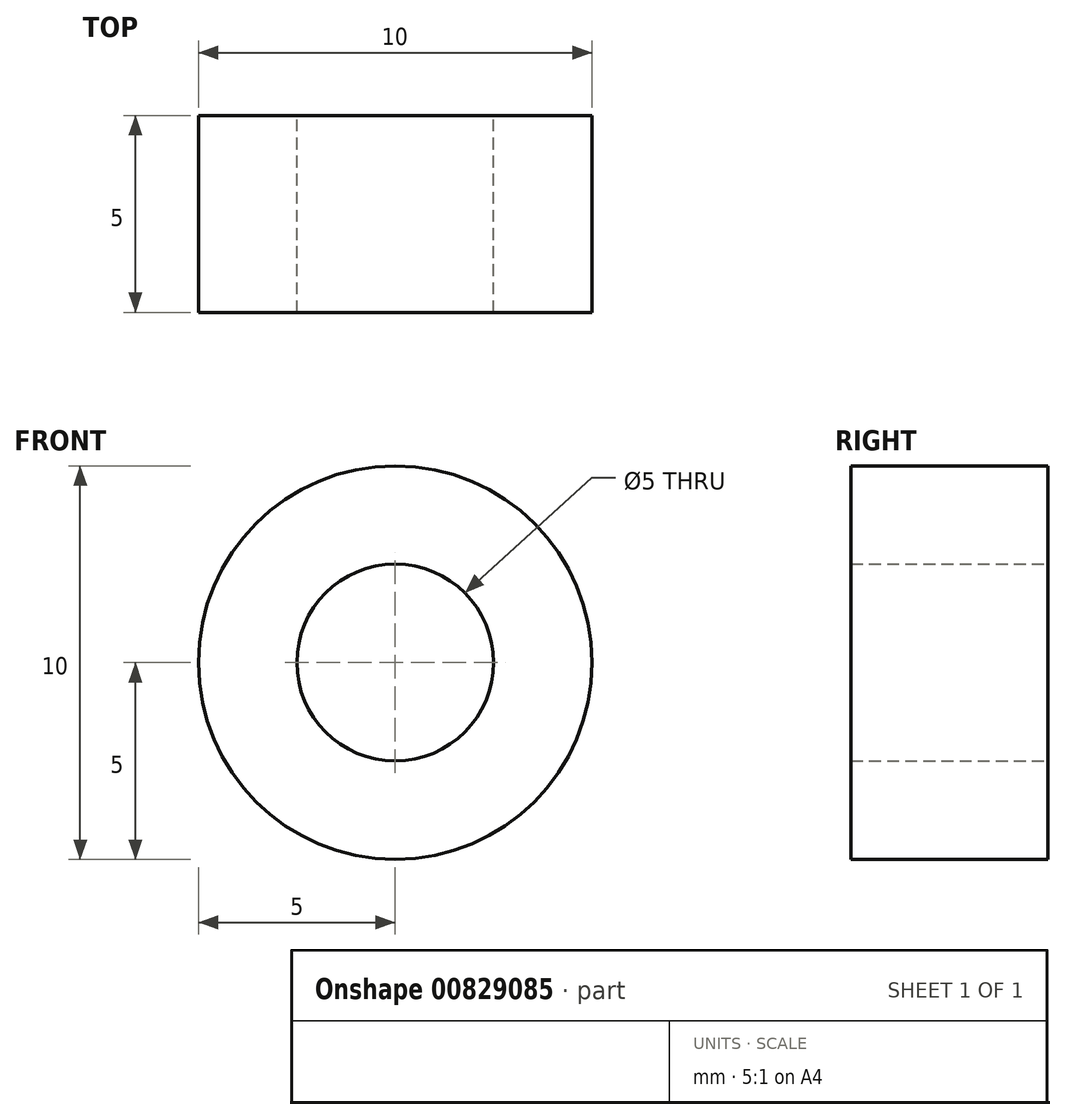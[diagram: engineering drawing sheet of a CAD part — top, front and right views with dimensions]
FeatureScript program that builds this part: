
annotation { "Feature Type Name" : "Feature", "Feature Type Description" : "" }
export const myFeature = defineFeature(function(context is Context, id is Id, definition is map)
    precondition{}
    {
        {
            var Q0;
            Q0=qCreatedBy(makeId("Front.planeOp"),FACE);
            var sketch = newSketch(context, id + "F0", { "sketchPlane" : qUnion([Q0])});
            skCircle(sketch, "E0", {"center": v(0, 0) * mm, "radius": 5 * mm});
            skCircle(sketch, "E1", {"center": v(0, 0) * mm, "radius": 2.5 * mm});
            skSolve(sketch);
        }
        {
            var Q0;
            Q0 = qSketchRegion(id + "F0", true);
            extrude(context, id + "F1", {"entities" : qUnion([Q0]), "depth" : 5 * mm, "offsetDistance" : 25 * mm});
        }
    });
